# Revit family: Post_Cap-K2_Stone-Newcastle-n1
name_source: partatom
category: Site
revit_build: Autodesk Revit Architecture 2013 (Build: 20130531_2115(x64)
units: mm (PartAtom-declared; Revit-internal decimal feet)

## types (1)
- Newcastle
    Default Elevation = 4' - 0"
    Description = Newcastle post caps are one solid piece of sandstone
    Finish = Stone-K2-Newcastle
    LEED = https://www.k2stone.com
    Length = 1' - 0"
    Manufacturer = K2 Stone
    Max Length = 4' - 0"
    Max Thickness = 0' - 8"
    Max Width = 2' - 0"
    Min Length = 1' - 0"
    Min Thickness = 0' - 2"
    Min Width = 1' - 0"
    Model = Newcastle Post Cap
    Product Documentation Link = https://www.k2stone.com
    Product Page URL = https://www.k2stone.com
    Requested Length = 1' - 0"
    Requested Thickness = 0' - 2"
    Requested Width = 1' - 0"
    Thickness = 0' - 2"
    Type Comments = Post Cap
    URL = https://www.k2stone.com
    Width = 1' - 0"

## geometry (parser evidence)
native form markers: Blend x4, Sweep x1
no freeform markers — native parametric forms only
